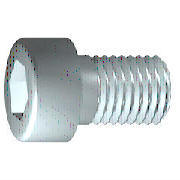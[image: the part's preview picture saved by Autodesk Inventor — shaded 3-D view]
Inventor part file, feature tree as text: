
AUTODESK INVENTOR PART (.ipt)
format: ipt  version: 2017 (Build 210142000, 142)  size: 193,536 bytes
history: native  units: mm (DEFAULTED — no unit token found)
features: sketch x2, extrude x1, plane x1, fillet x1
ambient origin geometry x7: Origin, YZ Plane, XY Plane, X Axis, Y Axis, Z Axis, Center Point
bodies: Solid1 (feature_tree), Body (feature_tree)
feature tree (5):
  extrude  "Slot"  Depth=4.0mm
  plane  "Work Plane1"
  fillet  "Fillet2"  Radius=4.0mm
  sketch  "Sketch1"  dims[d1=10.25mm d2=0.429515mm d3=4.0mm]
  sketch  "Sketch2"  dims[d4=2.0mm d5=60.0deg d6=4.0mm d7=4.0mm d8=3.464102mm d9=7.0mm d10=90.0deg d11=10.0mm d12=0.0mm d13=10.25mm d14=0.0mm d15=0.429415mm d16=0.429415mm d17=0.4mm d19=0.0mm d26=12.0mm d27=45.0deg d28=0.0mm d29=0.0mm d30=0.1mm]
